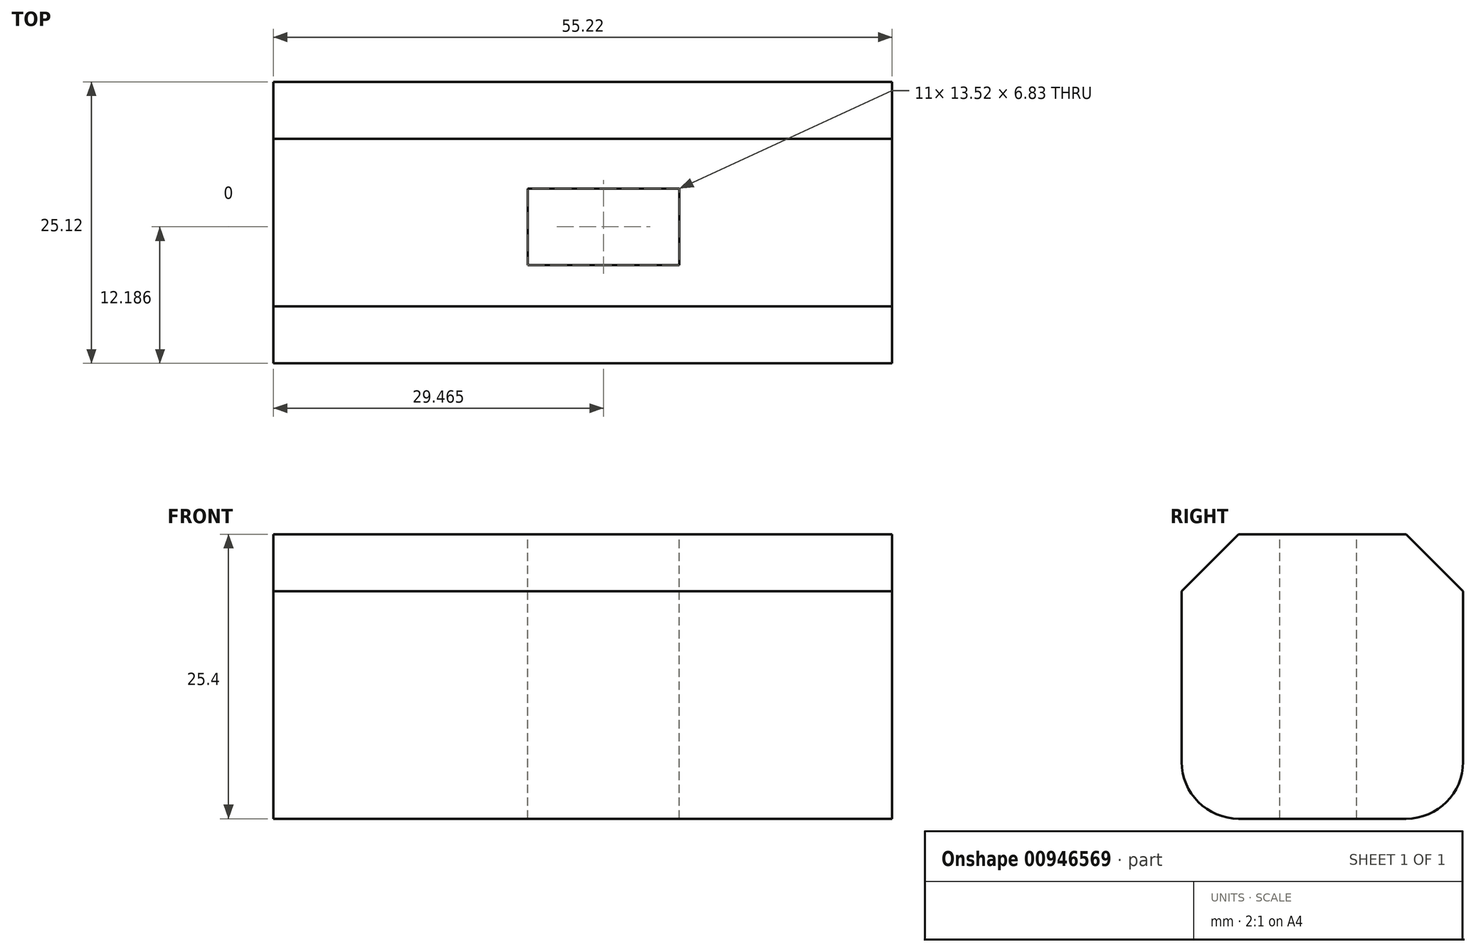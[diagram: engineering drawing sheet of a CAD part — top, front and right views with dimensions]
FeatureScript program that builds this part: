
annotation { "Feature Type Name" : "Feature", "Feature Type Description" : "" }
export const myFeature = defineFeature(function(context is Context, id is Id, definition is map)
    precondition{}
    {
        {
            var Q0;
            Q0=qCreatedBy(makeId("Top.planeOp"),FACE);
            var sketch = newSketch(context, id + "F0", { "sketchPlane" : qUnion([Q0])});
            skLineSegment(sketch, "E0.bottom", {"start": v(-20.68, 14.5) * mm, "end": v(34.54, 14.5) * mm});
            skLineSegment(sketch, "E0.top", {"start": v(-20.68, -10.61) * mm, "end": v(34.54, -10.61) * mm});
            skLineSegment(sketch, "E0.left", {"start": v(-20.68, 14.5) * mm, "end": v(-20.68, -10.61) * mm});
            skLineSegment(sketch, "E0.right", {"start": v(34.54, 14.5) * mm, "end": v(34.54, -10.61) * mm});
            skSolve(sketch);
        }
        {
            var Q0;
            Q0=makeQuery(id+"F0.imprint","IMPRINT",FACE,{"disambiguationData":[TD([[makeQuery(id+"F0.imprint","IMPRINT",EDGE,{"derivedFrom":sQuery(id+"F0.wireOp",EDGE,"E0.bottom")}),-1.0]])]});
            extrude(context, id + "F1", {"entities" : qUnion([Q0]), "depth" : 25.4 * mm, "offsetDistance" : 25.4 * mm});
        }
        {
            var Q0;
            Q0=makeQuery(id+"F1.opExtrude","CAP_FACE",FACE,{"disambiguationData":[OSD([sQuery(id+"F0.wireOp",EDGE,"E0.bottom"),sQuery(id+"F0.wireOp",EDGE,"E0.top"),sQuery(id+"F0.wireOp",EDGE,"E0.left"),sQuery(id+"F0.wireOp",EDGE,"E0.right")])],"isStart":false});
            var sketch = newSketch(context, id + "F2", { "sketchPlane" : qUnion([Q0])});
            skLineSegment(sketch, "E1.bottom", {"start": v(2.02, -1.84) * mm, "end": v(15.55, -1.84) * mm});
            skLineSegment(sketch, "E1.top", {"start": v(2.02, 5) * mm, "end": v(15.55, 5) * mm});
            skLineSegment(sketch, "E1.left", {"start": v(2.02, -1.84) * mm, "end": v(2.02, 5) * mm});
            skLineSegment(sketch, "E1.right", {"start": v(15.55, -1.84) * mm, "end": v(15.55, 5) * mm});
            skSolve(sketch);
        }
        {
            var Q0;
            Q0 = qSketchRegion(id + "F2", true);
            extrude(context, id + "F3", {"entities" : qUnion([Q0]), "operationType" : NewBodyOperationType.REMOVE, "oppositeDirection" : true, "depth" : 25.4 * mm, "offsetDistance" : 25.4 * mm});
        }
        {
            var Q0;
            Q0=makeQuery(id+"F1.opExtrude","CAP_EDGE",EDGE,{"disambiguationData":[OSD([sQuery(id+"F0.wireOp",EDGE,"E0.bottom")])],"isStart":false});
            var Q1;
            Q1=makeQuery(id+"F1.opExtrude","CAP_EDGE",EDGE,{"disambiguationData":[OSD([sQuery(id+"F0.wireOp",EDGE,"E0.top")])],"isStart":false});
            chamfer(context, id + "F4", {"entities" : qUnion([Q0, Q1]), "width" : 5.08 * mm, "tangentPropagation" : true});
        }
        {
            var Q0;
            Q0=makeQuery(id+"F1.opExtrude","CAP_EDGE",EDGE,{"disambiguationData":[OSD([sQuery(id+"F0.wireOp",EDGE,"E0.top")])],"isStart":true});
            var Q1;
            Q1=makeQuery(id+"F1.opExtrude","CAP_EDGE",EDGE,{"disambiguationData":[OSD([sQuery(id+"F0.wireOp",EDGE,"E0.bottom")])],"isStart":true});
            fillet(context, id + "F5", {"entities" : qUnion([Q0, Q1]), "radius" : 5.08 * mm, "tangentPropagation" : true, "allowEdgeOverflow" : false});
        }
    });
